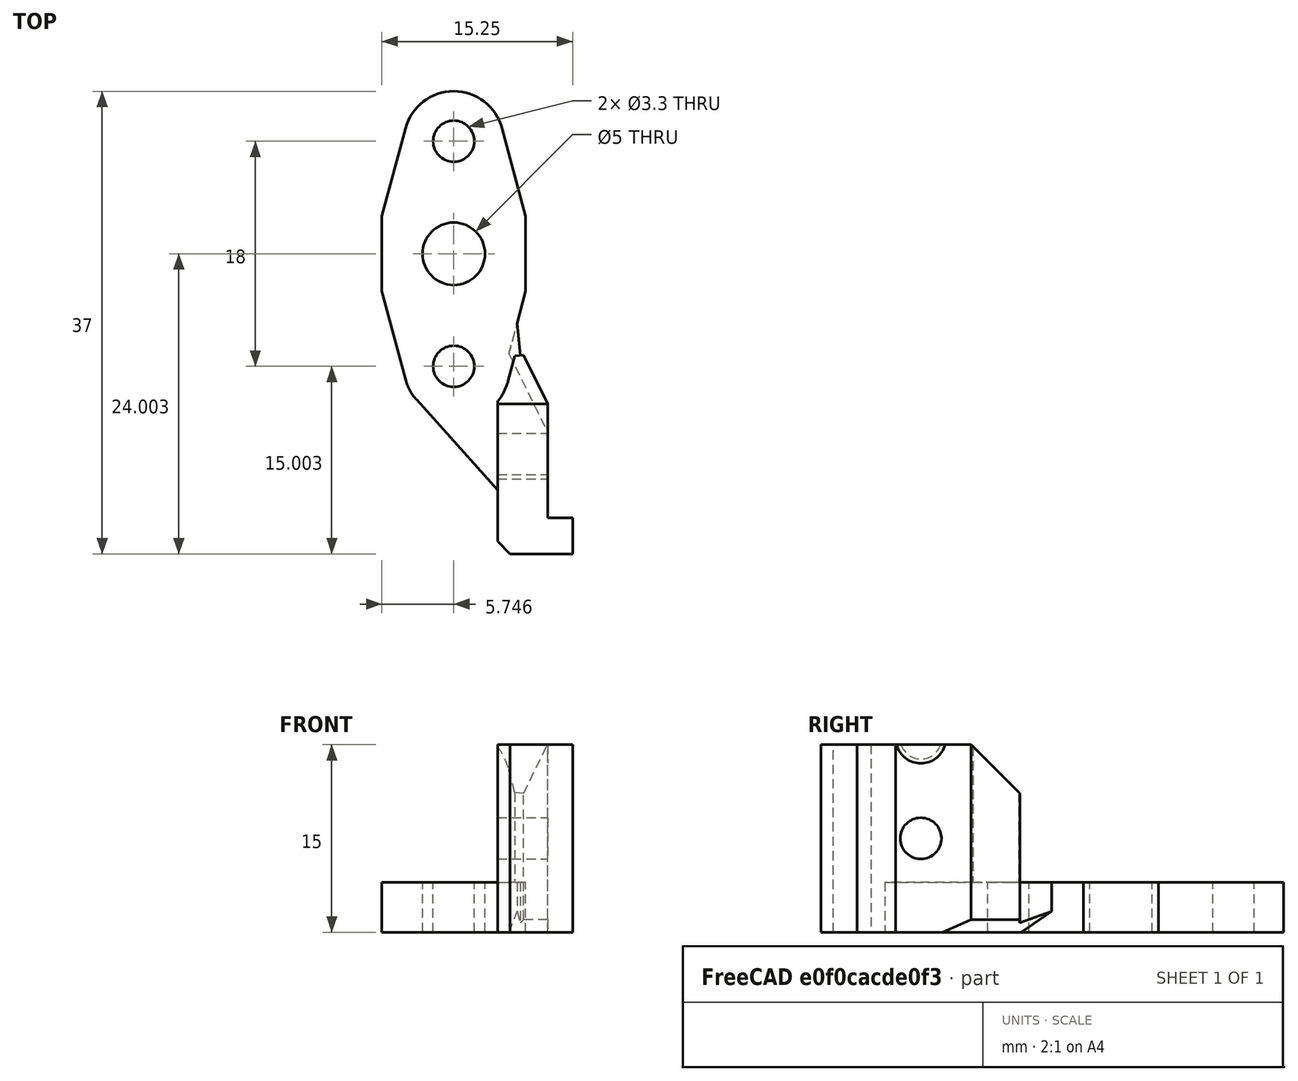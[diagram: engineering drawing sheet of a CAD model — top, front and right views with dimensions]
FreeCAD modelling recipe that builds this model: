
FCSTD DOCUMENT  (FreeCAD 0.19R24291 (Git))
Label: probe-mount-lighter
License: Other
LicenseURL: GPL3
objects: Part::Box×3, Part::Feature×2, Part::MultiFuse×2, Part::Chamfer×1, Part::Cylinder×1, Part::Cut×1
note: 10 computed .brp shape members not serialized (recipe doc carries the construction recipe); baked Part::Feature solids carry a one-line shape summary decoded from their .brp

FEATURE [Part::Box] Box  label="Cube"
  AttacherType = Attacher::AttachEngine3D
  Height = 19
  Length = 4
  Placement = pos=(-4,-8,0) rot=(0,0,1;0rad)
  Width = 6
FEATURE [Part::Feature] Defeatured001001
  shape: bbox 13.25 x 33 x 19 mm, 29 faces (baked)
FEATURE [Part::Box] Box001  label="Cube001"
  AttacherType = Attacher::AttachEngine3D
  Height = 19
  Length = 2
  Placement = pos=(0,-8,0) rot=(0,0,1;0rad)
  Width = 2.9
FEATURE [Part::Chamfer] Chamfer
  Base = -> Box
  Edges = 1 edges r=1: [Edge1]
FEATURE [Part::MultiFuse] Fusion
  Shapes = -> [Defeatured001001,Box001,Chamfer]
FEATURE [Part::Cylinder] Cylinder
  Angle = 360
  AttacherType = Attacher::AttachEngine3D
  Height = 4
  Placement = pos=(-4,0,15.5) rot=(0,1,0;1.5708rad)
  Radius = 2
FEATURE [Part::MultiFuse] Fusion001
  Shapes = -> [Fusion,Cylinder]
FEATURE [Part::Box] Box002  label="Cube002"
  AttacherType = Attacher::AttachEngine3D
  Height = 10
  Length = 10
  Placement = pos=(-5.5,-9.5,15) rot=(0,0,1;0rad)
  Width = 19
FEATURE [Part::Cut] Cut
  Base = -> Fusion001
  Tool = -> Box002
FEATURE [Part::Feature] Cut001
  shape: bbox 15.25 x 37 x 15 mm, 41 faces (baked)
